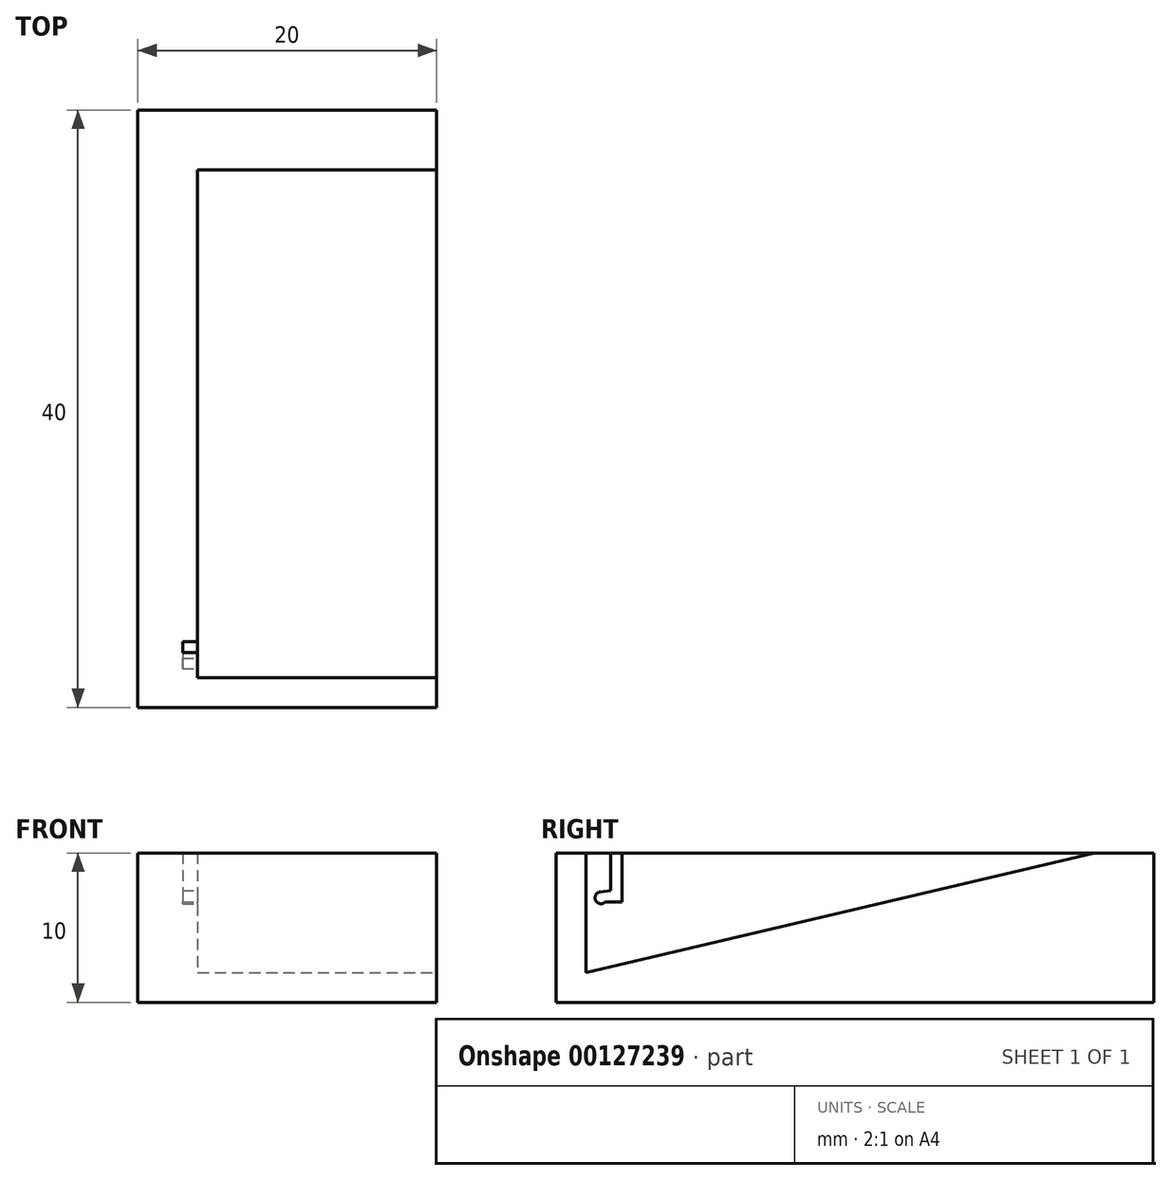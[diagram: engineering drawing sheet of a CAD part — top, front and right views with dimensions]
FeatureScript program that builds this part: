
annotation { "Feature Type Name" : "Feature", "Feature Type Description" : "" }
export const myFeature = defineFeature(function(context is Context, id is Id, definition is map)
    precondition{}
    {
        {
            var Q0;
            Q0=qCreatedBy(makeId("Top.planeOp"),FACE);
            var sketch = newSketch(context, id + "F0", { "sketchPlane" : qUnion([Q0])});
            skLineSegment(sketch, "E0.bottom", {"start": v(0, 0) * mm, "end": v(-20, 0) * mm});
            skLineSegment(sketch, "E0.top", {"start": v(0, 40) * mm, "end": v(-20, 40) * mm});
            skLineSegment(sketch, "E0.left", {"start": v(0, 0) * mm, "end": v(0, 40) * mm});
            skLineSegment(sketch, "E0.right", {"start": v(-20, 0) * mm, "end": v(-20, 40) * mm});
            skSolve(sketch);
        }
        {
            var Q0;
            Q0=makeQuery(id+"F0.imprint","IMPRINT",FACE,{"disambiguationData":[TD([[makeQuery(id+"F0.imprint","IMPRINT",EDGE,{"derivedFrom":sQuery(id+"F0.wireOp",EDGE,"E0.bottom")}),-1.0]])]});
            extrude(context, id + "F1", {"entities" : qUnion([Q0]), "depth" : 10 * mm});
        }
        {
            var Q0;
            Q0=makeQuery(id+"F1.opExtrude","SWEPT_FACE",FACE,{"disambiguationData":[OSD([sQuery(id+"F0.wireOp",EDGE,"E0.left")])]});
            var sketch = newSketch(context, id + "F2", { "sketchPlane" : qUnion([Q0])});
            skLineSegment(sketch, "E1", {"start": v(36, 10) * mm, "end": v(2, 2) * mm});
            skLineSegment(sketch, "E2", {"start": v(2, 2) * mm, "end": v(2, 10) * mm});
            skLineSegment(sketch, "E3.0", {"start": v(2, 10) * mm, "end": v(36, 10) * mm});
            skPoint(sketch, "E4.orphan", {"position": v(0, 10) * mm});
            skPoint(sketch, "E5.orphan", {"position": v(40, 10) * mm});
            skSolve(sketch);
        }
        {
            var Q0;
            Q0=makeQuery(id+"F2.imprint","IMPRINT",FACE,{"disambiguationData":[TD([[makeQuery(id+"F2.imprint","IMPRINT",EDGE,{"derivedFrom":sQuery(id+"F2.wireOp",EDGE,"E1")}),-1.0]])]});
            extrude(context, id + "F3", {"entities" : qUnion([Q0]), "operationType" : NewBodyOperationType.REMOVE, "oppositeDirection" : true, "depth" : 16 * mm});
        }
        {
            var Q0;
            Q0=makeQuery(id+"F3.boolean.opBoolean","COPY",FACE,{"derivedFrom":makeQuery(id+"F3.opExtrude","CAP_FACE",FACE,{"disambiguationData":[OSD([sQuery(id+"F2.wireOp",EDGE,"E1"),sQuery(id+"F2.wireOp",EDGE,"E2"),sQuery(id+"F2.wireOp",EDGE,"E3.0")])],"isStart":false})});
            var sketch = newSketch(context, id + "F4", { "sketchPlane" : qUnion([Q0])});
            skPoint(sketch, "E6.start.orphan", {"position": v(4.4, 10) * mm});
            skPoint(sketch, "E7.start.orphan", {"position": v(3.65, 10) * mm});
            skLineSegment(sketch, "E8", {"start": v(3.65, 10) * mm, "end": v(3.65, 7.47) * mm});
            skLineSegment(sketch, "E9", {"start": v(3.65, 10) * mm, "end": v(4.4, 10) * mm});
            skLineSegment(sketch, "E10", {"start": v(4.4, 10) * mm, "end": v(4.4, 6.72) * mm});
            skLineSegment(sketch, "E11", {"start": v(3.65, 7.47) * mm, "end": v(2.96, 7.4) * mm});
            skLineSegment(sketch, "E12", {"start": v(4.4, 6.72) * mm, "end": v(3.29, 6.72) * mm});
            skArc(sketch, "E13", {"start": v(2.96, 7.4) * mm, "mid": v(2.64, 6.82) * mm, "end": v(3.29, 6.72) * mm});
            skPoint(sketch, "E14.end.orphan", {"position": v(3.35, 7.4) * mm});
            skSolve(sketch);
        }
        {
            var Q0;
            Q0=makeQuery(id+"F4.imprint","IMPRINT",FACE,{"disambiguationData":[TD([[makeQuery(id+"F4.imprint","IMPRINT",EDGE,{"derivedFrom":sQuery(id+"F4.wireOp",EDGE,"E8")}),1.0]])]});
            extrude(context, id + "F5", {"entities" : qUnion([Q0]), "operationType" : NewBodyOperationType.REMOVE, "oppositeDirection" : true, "depth" : 1 * mm});
        }
    });
